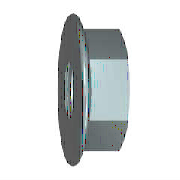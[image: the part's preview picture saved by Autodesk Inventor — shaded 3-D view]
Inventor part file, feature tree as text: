
AUTODESK INVENTOR PART (.ipt)
format: ipt  version: 2022 (Build 260153000, 153)  size: 204,800 bytes
history: native  units: mm (DEFAULTED — no unit token found)
features: sketch x3, other x2, chamfer x1, hole x1, plane x1
ambient origin geometry x7: Origin, YZ Plane, XZ Plane, X Axis, Y Axis, Z Axis, Center Point
bodies: Solid1 (feature_tree), Body (feature_tree)
feature tree (8):
  other  "Ring"
  chamfer  "Chamfer1"  Distance=21.8mm
  hole  "Thread"  [1 undecoded]
  other  "Work Axis1"
  plane  "Work Plane1"
  sketch  "Sketch1"  dims[d3=1.5mm d4=21.8mm]
  sketch  "Sketch3"  dims[d8=90.0deg]
  sketch  "Sketch4"  dims[d5=1.5mm d6=17.320508mm d7=10.0mm d9=0.0mm d10=30.0deg d11=15.0mm d24=90.0deg d25=8.376mm d26=6.0mm d27=4.0mm d28=2.0mm d29=14.3117mm d30=8.0mm d31=20.594885mm d12=0.811899mm d13=30.0deg d15=10.0mm d16=4.363323mm d45=0.0mm d46=0.811899mm d47=0.0mm d49=0.0mm d51=0.811899mm d52=2.0mm d53=45.0deg d54=0.0mm]
note: 1 required parameter value undecoded (feature->parameter linkage not recoverable at this tier; creation-order binding heuristic only, values carry confidence <= 0.55)
